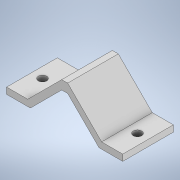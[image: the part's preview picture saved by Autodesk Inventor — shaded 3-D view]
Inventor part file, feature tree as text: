
AUTODESK INVENTOR PART (.ipt)
format: ipt  version: 2022 (Build 260153000, 153)  size: 273,408 bytes
history: native  units: mm
features: sketch x2, extrude x1, hole x1, chamfer x1
ambient origin geometry x8: Origin, YZ Plane, XZ Plane, XY Plane, X Axis, Y Axis, Z Axis, Center Point
bodies: Body1 (feature_tree)
feature tree (5):
  extrude  "Extrusion2"  TaperAngle=45.0deg  [1 undecoded]
  hole  "Hole1"  [1 undecoded]
  chamfer  "Chamfer1"  Distance=3.0mm
  sketch  "Sketch1"  dims[d34=23.0mm d35=45.0deg]
  sketch  "Sketch3"  dims[d36=23.0mm d37=3.0mm d38=3.0mm d39=45.0deg d41=6.0mm d49=10.0mm d50=6.0mm d51=3.0mm d52=10.0mm d53=24.0mm d54=0.0mm d55=12.0mm d56=12.0mm d57=5.0mm d58=5.0mm d59=4.0mm d60=16.0mm d61=4.0mm d62=2.0mm d63=90.0deg d64=8.0mm d65=20.594885mm d66=2.0mm d67=2.0mm d68=45.0deg]
note: 2 required parameter values undecoded (feature->parameter linkage not recoverable at this tier; creation-order binding heuristic only, values carry confidence <= 0.55)
